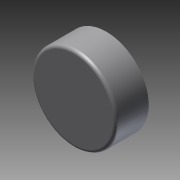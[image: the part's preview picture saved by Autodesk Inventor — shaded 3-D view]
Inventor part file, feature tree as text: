
AUTODESK INVENTOR PART (.ipt)
format: ipt  version: 2012 SP1 (Build 160190100, 190)  size: 87,040 bytes
history: native  units: in
note: dims shown in document units (in); Inventor stores cm internally (conversion verified against a paired STEP export)
features: extrude x1, fillet x1, sketch x1
ambient origin geometry x8: Origin, YZ Plane, XZ Plane, XY Plane, X Axis, Y Axis, Z Axis, Center Point
bodies: Solid1 (feature_tree)
feature tree (3):
  extrude  "Extrusion1"  Depth=0.1in TaperAngle=0.0deg
  fillet  "Fillet1"  Radius=0.01in
  sketch  "Sketch1"  dims[d0=0.26in d1=0.1in d2=0.0in d3=0.01in]
